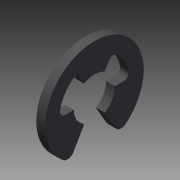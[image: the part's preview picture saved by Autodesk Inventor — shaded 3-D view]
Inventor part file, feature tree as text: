
AUTODESK INVENTOR PART (.ipt)
format: ipt  version: 2014 (Build 180170000, 170)  size: 120,832 bytes
history: native  units: in
note: dims shown in document units (in); Inventor stores cm internally (conversion verified against a paired STEP export)
features: other x7, extrude x1, sketch x1
ambient origin geometry x8: Origin, YZ Plane, XZ Plane, XY Plane, X Axis, Y Axis, Z Axis, Center Point
bodies: Solid1 (feature_tree)
feature tree (9):
  extrude  "Extrusion1"  [1 undecoded]
  other  "rr_XY"
  other  "rr_YZ"
  other  "rr_ZX"
  other  "rr_X"
  other  "rr_Y"
  other  "rr_Z"
  other  "rr_Center"
  sketch  "Sketch_1"  dims[d0=0.025in d1=0.0in]
note: 1 required parameter value undecoded (feature->parameter linkage not recoverable at this tier; creation-order binding heuristic only, values carry confidence <= 0.55)
